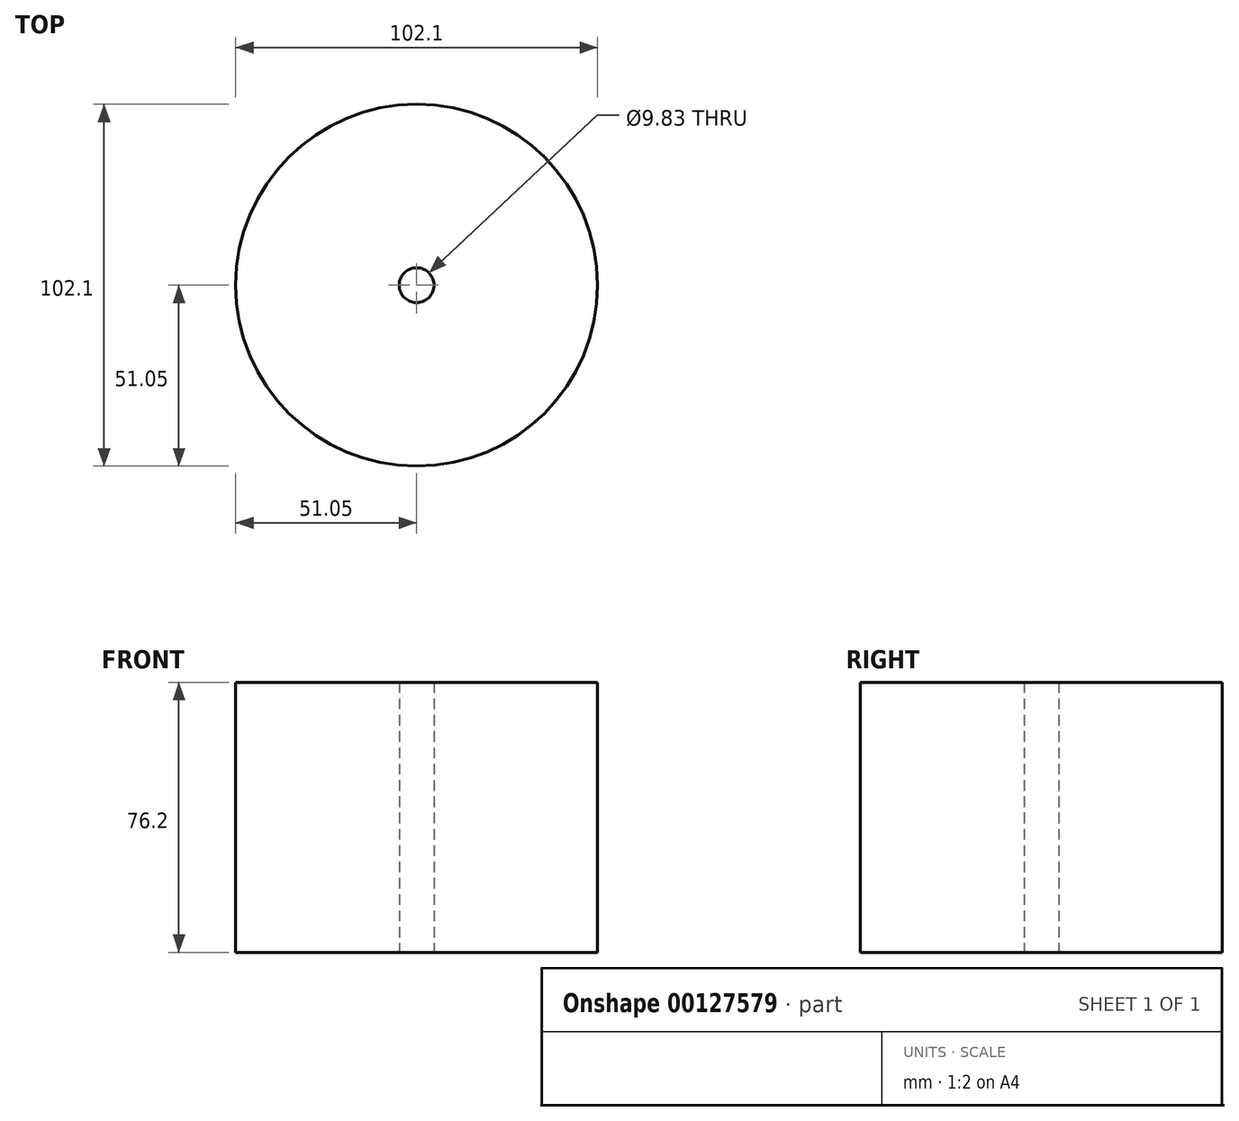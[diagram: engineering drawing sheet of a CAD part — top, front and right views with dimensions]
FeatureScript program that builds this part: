
annotation { "Feature Type Name" : "Feature", "Feature Type Description" : "" }
export const myFeature = defineFeature(function(context is Context, id is Id, definition is map)
    precondition{}
    {
        {
            var Q0;
            Q0=qCreatedBy(makeId("Top.planeOp"),FACE);
            var sketch = newSketch(context, id + "F0", { "sketchPlane" : qUnion([Q0])});
            skCircle(sketch, "E0", {"center": v(0, 0) * mm, "radius": 51.05 * mm});
            skSolve(sketch);
        }
        {
            var Q0;
            Q0=makeQuery(id+"F0.imprint","IMPRINT",FACE,{"disambiguationData":[TD([[makeQuery(id+"F0.imprint","IMPRINT",EDGE,{"derivedFrom":sQuery(id+"F0.wireOp",EDGE,"E0")}),1.0]])]});
            extrude(context, id + "F1", {"entities" : qUnion([Q0]), "depth" : 76.2 * mm});
        }
        {
            var Q0;
            Q0=qCreatedBy(makeId("Top.planeOp"),FACE);
            var sketch = newSketch(context, id + "F2", { "sketchPlane" : qUnion([Q0])});
            skCircle(sketch, "E1", {"center": v(0, 0) * mm, "radius": 4.85 * mm});
            skSolve(sketch);
        }
        {
            var Q0;
            Q0=sQuery(id+"F2.wireOp",VERTEX,"E1.center");
            var Q1;
            Q1=makeQuery(id+"F1.opExtrude","SWEPT_BODY",BODY,{"disambiguationData":[OSD([sQuery(id+"F0.wireOp",EDGE,"E0")])]});
            hole(context, id + "F3", {"style" : HoleStyle.SIMPLE, "endStyle" : HoleEndStyle.THROUGH, "oppositeDirection" : true, "holeDiameter" : 9.83 * mm, "locations" : qUnion([Q0]), "scope" : qUnion([Q1]), "isTappedThrough" : true});
        }
    });
